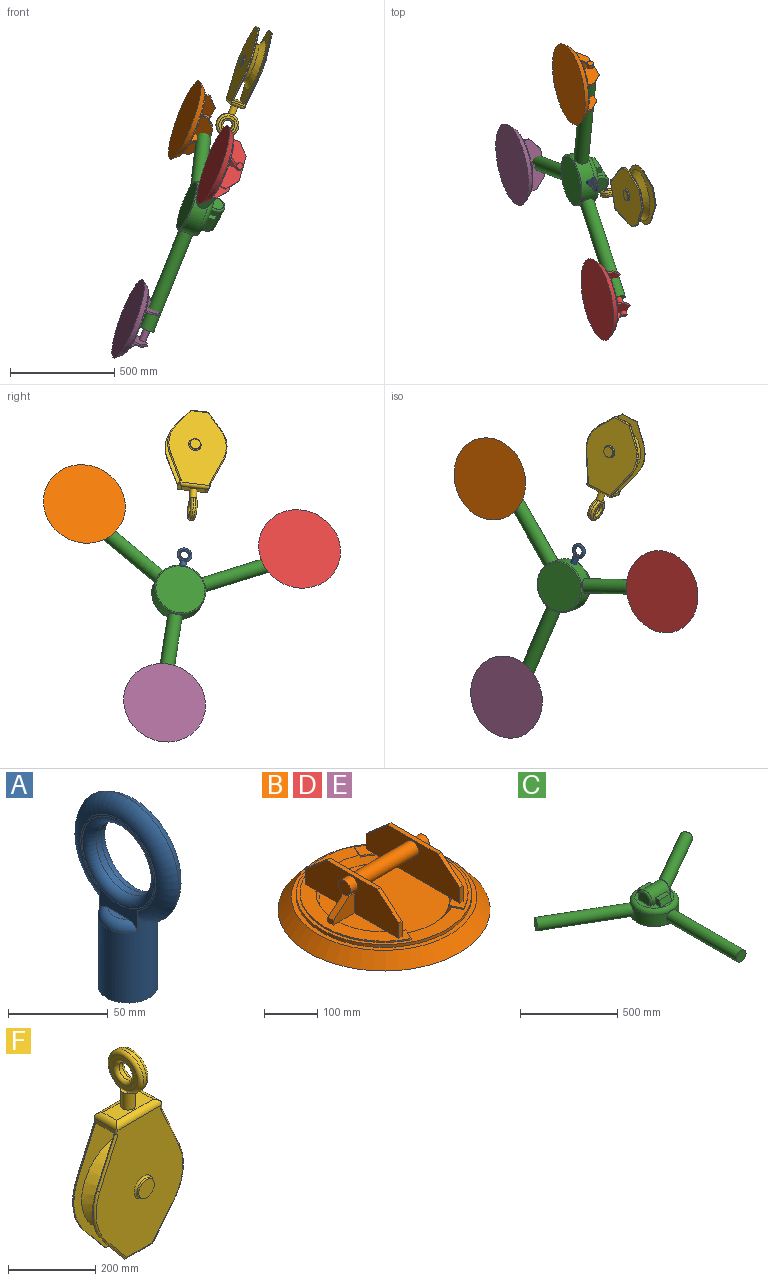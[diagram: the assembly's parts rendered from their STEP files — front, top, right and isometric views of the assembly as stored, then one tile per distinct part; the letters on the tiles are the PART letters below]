
ASSEMBLY  parts=6 mates=6
PART A: 13 faces, bbox 32.5x79x118.5 mm
  f0: plane 14.48x3.1mm, normal (0,0,1), area 31mm2, adj f5,f10
  f1: cylinder r=15mm len=56.07mm, axis (0,0,-1), area 4201.7mm2, adj f3,f4,f5,f7,f8,f9,f10
  f2: plane 14.48x3.1mm, normal (0,0,1), area 31mm2, adj f4,f9
  f3: plane 30x30mm, normal (0,0,-1), area 706.9mm2, adj f1
  f4: plane 62.82x53.03mm, normal (1,0,0), area 344.9mm2, adj f1,f2,f7,f9,f12
  f5: plane 62.82x53.03mm, normal (-1,0,0), area 344.8mm2, adj f0,f1,f8,f10,f11
  f6: cylinder r=20.45mm len=40.9mm, axis (-1,0,0), area 488.3mm2, adj f11,f12
  f7: torus R=26.52mm, axis (1,0,0), area 2157.2mm2, adj f1,f4,f8
  f8: torus R=26.52mm, axis (1,0,0), area 2157.2mm2, adj f1,f5,f7
  f9: torus R=10mm, axis (0,0,1), area 210.8mm2, adj f1,f2,f4
  f10: torus R=10mm, axis (0,0,1), area 210.8mm2, adj f0,f1,f5
  f11: torus R=25.45mm, axis (1,0,0), area 1098.8mm2, adj f5,f6
  f12: torus R=25.45mm, axis (1,0,0), area 1098.8mm2, adj f4,f6
PART B: 50 faces, bbox 400x400x123.8 mm
  f0: plane 34.67x9.11mm, normal (0,1,0), area 316mm2, adj f2,f3,f4,f19
  f1: plane 34.67x9.11mm, normal (0,-1,0), area 316mm2, adj f2,f3,f4,f20
  f2: plane 249.76x84.24mm, normal (1,0,0), area 16662.5mm2, adj f0,f1,f4,f17,f18,f19,f20,f23
  f3: plane 249.76x84.24mm, normal (-1,0,0), area 17354.3mm2, adj f0,f1,f4,f17,f18,f19,f20,f45
  f4: plane 286.37x105.25mm, normal (0,0,1), area 9032.7mm2, adj f0,f1,f2,f3,f12,f13,f14,f15
  f5: plane 330.98x330.98mm, normal (0,0,1), area 13326.7mm2, adj f6,f11,f12,f13,f14,f31,f32,f33
  f6: cone r=134.59mm half-angle=37deg, axis (0,0,1), area 15653.4mm2, adj f5,f7,f16,f35
  f7: plane 245.92x245.92mm, normal (0,0,1), area 47497.9mm2, adj f6
  f8: plane 400x400mm, normal (0,0,-1), area 125663.7mm2, adj f9
  f9: cone r=200mm half-angle=39.8deg, axis (0,0,-1), area 46006.2mm2, adj f8,f10
  f10: plane 350x350mm, normal (0,0,1), area 10175.1mm2, adj f9,f11
  f11: cylinder r=165.49mm len=330.98mm, axis (0,0,1), area 6841.3mm2, adj f5,f10
  f12: plane 26.9x13.27mm, normal (-0.9,-0.44,0), area 90mm2, adj f4,f5,f13,f15,f16
  f13: cylinder r=158.49mm len=286.37mm, axis (0,0,-1), area 1072.7mm2, adj f4,f5,f12,f14
  f14: plane 27.3x12.43mm, normal (-0.91,0.41,0), area 90mm2, adj f4,f5,f13,f15,f16
  f15: cylinder r=128.49mm len=232.17mm, axis (0,0,-1), area 869.6mm2, adj f4,f12,f14,f16,f17
  f16: plane 243.19x81.35mm, normal (0,0,-1), area 1811.1mm2, adj f6,f12,f14,f15
  f17: plane 206x51.68mm, normal (0,0,-1), area 2448.9mm2, adj f2,f3,f15,f24,f25
  f18: plane 134.61x9.11mm, normal (0,0,1), area 1226.8mm2, adj f2,f3,f19,f20
  f19: plane 57.58x49.57mm, normal (0,0.65,0.76), area 692.4mm2, adj f0,f2,f3,f18
  f20: plane 57.58x49.57mm, normal (0,-0.65,0.76), area 692.4mm2, adj f1,f2,f3,f18
  f21: plane 15x10.68mm, normal (1,0,0), area 160.2mm2, adj f4,f22,f24,f25
  f22: plane 41.45x35.44mm, normal (0.65,0,0.76), area 818mm2, adj f21,f23,f24,f25
  f23: plane 15.31x15mm, normal (0,0,1), area 229.7mm2, adj f2,f22,f24,f25
  f24: plane 56.76x46.12mm, normal (0,-1,0), area 1883.2mm2, adj f2,f4,f17,f21,f22,f23
  f25: plane 56.76x46.12mm, normal (0,1,0), area 1883.2mm2, adj f2,f4,f17,f21,f22,f23
  f26: plane 34.67x9.11mm, normal (0,1,0), area 316mm2, adj f28,f29,f30,f38
  f27: plane 34.67x9.11mm, normal (0,-1,0), area 316mm2, adj f28,f29,f30,f39
  f28: plane 249.76x84.24mm, normal (-1,0,0), area 16662.5mm2, adj f26,f27,f30,f36,f37,f38,f39,f42
  f29: plane 249.76x84.24mm, normal (1,0,0), area 17354.3mm2, adj f26,f27,f30,f36,f37,f38,f39,f45
  f30: plane 286.37x105.25mm, normal (0,0,1), area 9032.7mm2, adj f26,f27,f28,f29,f31,f32,f33,f34
  f31: plane 26.9x13.27mm, normal (0.9,-0.44,0), area 90mm2, adj f5,f30,f32,f34,f35
  f32: cylinder r=158.49mm len=286.37mm, axis (0,0,-1), area 1072.7mm2, adj f5,f30,f31,f33
  f33: plane 27.3x12.43mm, normal (0.91,0.41,0), area 90mm2, adj f5,f30,f32,f34,f35
  f34: cylinder r=128.49mm len=232.17mm, axis (0,0,-1), area 869.6mm2, adj f30,f31,f33,f35,f36
  f35: plane 243.19x81.35mm, normal (0,0,-1), area 1811.1mm2, adj f6,f31,f33,f34
  f36: plane 206x51.68mm, normal (0,0,-1), area 2448.9mm2, adj f28,f29,f34,f43,f44
  f37: plane 134.61x9.11mm, normal (0,0,1), area 1226.8mm2, adj f28,f29,f38,f39
  f38: plane 57.58x49.57mm, normal (0,0.65,0.76), area 692.4mm2, adj f26,f28,f29,f37
  f39: plane 57.58x49.57mm, normal (0,-0.65,0.76), area 692.4mm2, adj f27,f28,f29,f37
  f40: plane 15x10.68mm, normal (-1,0,0), area 160.2mm2, adj f30,f41,f43,f44
  f41: plane 41.45x35.44mm, normal (-0.65,0,0.76), area 818mm2, adj f40,f42,f43,f44
  f42: plane 15.31x15mm, normal (0,0,1), area 229.7mm2, adj f28,f41,f43,f44
  f43: plane 56.76x46.12mm, normal (0,-1,0), area 1883.2mm2, adj f28,f30,f36,f40,f41,f42
  f44: plane 56.76x46.12mm, normal (0,1,0), area 1883.2mm2, adj f28,f30,f36,f40,f41,f42
  f45: cylinder r=16.26mm len=153.62mm, axis (-1,0,0), area 15695.3mm2, adj f3,f29
  f46: plane 32.52x32.52mm, normal (-1,0,0), area 830.7mm2, adj f47
  f47: cylinder r=16.26mm len=32.52mm, axis (-1,0,0), area 2051.1mm2, adj f28,f46
  f48: cylinder r=16.26mm len=32.52mm, axis (-1,0,0), area 2051.1mm2, adj f2,f49
  f49: plane 32.52x32.52mm, normal (1,0,0), area 830.7mm2, adj f48
PART C: 24 faces, bbox 1125.9x975.1x175.1 mm
  f0: cylinder r=125mm len=250mm, axis (0,0,-1), area 44515.2mm2, adj f1,f4,f6,f20,f22
  f1: torus R=100mm, axis (0,0,1), area 28361.9mm2, adj f0,f2,f6,f20,f22
  f2: plane 200x200mm, normal (0,0,1), area 11368.9mm2, adj f1,f8,f9,f10,f11,f13,f14,f15
  f3: plane 240x240mm, normal (0,0,-1), area 45238.9mm2, adj f4
  f4: torus R=120mm, axis (0,0,1), area 6078.8mm2, adj f0,f3
  f5: plane 69.5x69.5mm, normal (0,-1,0), area 3793.5mm2, adj f6
  f6: cylinder r=34.75mm len=509.93mm, axis (0,1,0), area 110799.7mm2, adj f0,f1,f5
  f7: plane 78x27.87mm, normal (0,0,1), area 2174.1mm2, adj f8,f9,f10,f11
  f8: plane 78x36.94mm, normal (0,-0.94,0.33), area 3056.5mm2, adj f2,f7,f9,f10
  f9: plane 42.16x36.94mm, normal (1,0,0), area 1205.7mm2, adj f2,f7,f8,f11
  f10: plane 42.16x36.94mm, normal (-1,0,0), area 1205.7mm2, adj f2,f7,f8,f11
  f11: cylinder r=50mm len=128mm, axis (-1,0,0), area 19467.6mm2, adj f2,f7,f9,f10,f12,f14,f15,f18
  f12: plane 78x27.87mm, normal (0,0,1), area 2174.1mm2, adj f11,f13,f14,f15
  f13: plane 78x36.94mm, normal (0,0.94,0.33), area 3056.5mm2, adj f2,f12,f14,f15
  f14: plane 42.16x36.94mm, normal (1,0,0), area 1205.7mm2, adj f2,f11,f12,f13
  f15: plane 42.16x36.94mm, normal (-1,0,0), area 1205.7mm2, adj f2,f11,f12,f13
  f16: plane 80x60mm, normal (1,0,0), area 4043.9mm2, adj f2,f19
  f17: plane 80x60mm, normal (-1,0,0), area 4043.9mm2, adj f2,f18
  f18: torus R=40mm, axis (1,0,0), area 2938.1mm2, adj f2,f11,f17
  f19: torus R=40mm, axis (1,0,0), area 2938.1mm2, adj f2,f11,f16
  f20: cylinder r=34.75mm len=476.36mm, axis (0.87,-0.5,0), area 110799.6mm2, adj f0,f1,f21
  f21: plane 69.5x60.19mm, normal (-0.87,0.5,0), area 3793.5mm2, adj f20
  f22: cylinder r=34.75mm len=476.36mm, axis (-0.87,-0.5,0), area 110799.7mm2, adj f0,f1,f23
  f23: plane 69.5x60.19mm, normal (0.87,0.5,0), area 3793.5mm2, adj f22
PART D: same geometry as B
PART E: same geometry as B
PART F: 67 faces, bbox 313.9x118.5x549.6 mm
  f0: cylinder r=54.75mm len=31.96mm, axis (-1,0,0), area 278.3mm2, adj f2,f8
  f1: cylinder r=54.75mm len=31.96mm, axis (-1,0,0), area 278.3mm2, adj f2,f10
  f2: cylinder r=16.74mm len=47.87mm, axis (0,0,-1), area 4897.8mm2, adj f0,f1,f3,f42
  f3: cylinder r=54.75mm len=109.5mm, axis (-1,0,0), area 3105.1mm2, adj f2,f8,f10
  f4: cylinder r=23.34mm len=46.68mm, axis (-1,0,0), area 1466.5mm2, adj f7,f9
  f5: plane 89.5x89.5mm, normal (1,0,0), area 2799.5mm2, adj f9,f10
  f6: plane 89.5x89.5mm, normal (-1,0,0), area 2799.5mm2, adj f7,f8
  f7: torus R=33.34mm, axis (1,0,0), area 2662.2mm2, adj f4,f6
  f8: torus R=44.75mm, axis (1,0,0), area 5045.1mm2, adj f0,f3,f6
  f9: torus R=33.34mm, axis (1,0,0), area 2662.2mm2, adj f4,f5
  f10: torus R=44.75mm, axis (1,0,0), area 5045.1mm2, adj f1,f3,f5
  f11: plane 250x250mm, normal (0,1,0), area 47087mm2, adj f14,f36
  f12: plane 250x250mm, normal (0,-1,0), area 47087mm2, adj f13,f24
  f13: cone r=125mm half-angle=54.5deg, axis (0,-1,0), area 29199.9mm2, adj f12,f14
  f14: cone r=125mm half-angle=54.5deg, axis (0,1,0), area 29199.9mm2, adj f11,f13
  f15: plane 131.07x58.17mm, normal (-0.91,0,0.41), area 286.8mm2, adj f16,f23,f41,f48
  f16: cylinder r=145mm len=150.44mm, axis (0,1,0), area 319.5mm2, adj f15,f17,f23,f49
  f17: plane 83.79x68.31mm, normal (-0.78,0,-0.63), area 216.2mm2, adj f16,f18,f23,f50
  f18: plane 88.15x2mm, normal (0,0,-1), area 176.3mm2, adj f17,f19,f23,f51
  f19: plane 83.79x68.31mm, normal (0.78,0,-0.63), area 216.2mm2, adj f18,f20,f23,f52
  f20: cylinder r=145mm len=150.44mm, axis (0,1,0), area 319.5mm2, adj f19,f21,f23,f53
  f21: plane 131.07x58.17mm, normal (0.91,0,0.41), area 286.8mm2, adj f20,f23,f40,f54
  f22: plane 370.3x280mm, normal (0,-1,0), area 75486.2mm2, adj f44,f47,f48,f49,f50,f51,f52,f53
  f23: plane 365.3x290mm, normal (0,1,0), area 79482.6mm2, adj f15,f16,f17,f18,f19,f20,f21,f24
  f24: cylinder r=25.23mm len=50.47mm, axis (0,1,0), area 773.3mm2, adj f12,f23
  f25: plane 50.47x50.47mm, normal (0,-1,0), area 2000.4mm2, adj f26
  f26: cylinder r=25.23mm len=50.47mm, axis (0,1,0), area 792.7mm2, adj f25,f66
  f27: plane 131.07x58.17mm, normal (-0.91,0,0.41), area 286.8mm2, adj f28,f35,f41,f57
  f28: cylinder r=145mm len=150.44mm, axis (0,-1,0), area 319.5mm2, adj f27,f29,f35,f58
  f29: plane 83.79x68.31mm, normal (-0.78,0,-0.63), area 216.2mm2, adj f28,f30,f35,f59
  f30: plane 88.15x2mm, normal (0,0,-1), area 176.3mm2, adj f29,f31,f35,f60
  f31: plane 83.79x68.31mm, normal (0.78,0,-0.63), area 216.2mm2, adj f30,f32,f35,f61
  f32: cylinder r=145mm len=150.44mm, axis (0,-1,0), area 319.5mm2, adj f31,f33,f35,f62
  f33: plane 131.07x58.17mm, normal (0.91,0,0.41), area 286.8mm2, adj f32,f35,f40,f63
  f34: plane 370.3x280mm, normal (0,1,0), area 75486.2mm2, adj f45,f56,f57,f58,f59,f60,f61,f62
  f35: plane 365.3x290mm, normal (0,-1,0), area 79482.6mm2, adj f27,f28,f29,f30,f31,f32,f33,f36
  f36: cylinder r=25.23mm len=50.47mm, axis (0,-1,0), area 773.3mm2, adj f11,f35
  f37: plane 50.47x50.47mm, normal (0,1,0), area 2000.4mm2, adj f38
  f38: cylinder r=25.23mm len=50.47mm, axis (0,-1,0), area 792.7mm2, adj f37,f65
  f39: plane 148.73x60mm, normal (0,0,-1), area 8924mm2, adj f23,f35,f40,f41
  f40: plane 64x10mm, normal (1,0,0), area 640mm2, adj f21,f33,f39,f43,f55,f64
  f41: plane 64x10mm, normal (-1,0,0), area 640mm2, adj f15,f27,f39,f46,f47,f56
  f42: plane 118.73x44mm, normal (0,0,1), area 4343.4mm2, adj f2,f43,f44,f45,f46
  f43: cylinder r=15mm len=71.07mm, axis (0,-1,0), area 1451.2mm2, adj f40,f42,f44,f45,f55,f64
  f44: cylinder r=15mm len=145.81mm, axis (1,0,0), area 3212.1mm2, adj f22,f42,f43,f46,f47,f55
  f45: cylinder r=15mm len=145.81mm, axis (1,0,0), area 3212.1mm2, adj f34,f42,f43,f46,f56,f64
  f46: cylinder r=15mm len=71.07mm, axis (0,1,0), area 1451.2mm2, adj f41,f42,f44,f45,f47,f56
  f47: cylinder r=5mm len=17.52mm, axis (0,0,-1), area 107.6mm2, adj f22,f41,f44,f46,f48
  f48: cylinder r=5mm len=134.07mm, axis (0.41,0,0.91), area 1129.3mm2, adj f15,f22,f47,f49
  f49: torus R=140mm, axis (0,-1,0), area 1238.9mm2, adj f16,f22,f48,f50
  f50: cylinder r=5mm len=86.95mm, axis (-0.63,0,0.78), area 842.3mm2, adj f17,f22,f49,f51
  f51: cylinder r=5mm len=88.15mm, axis (-1,0,0), area 678.8mm2, adj f18,f22,f50,f52
  f52: cylinder r=5mm len=86.95mm, axis (-0.63,0,-0.78), area 842.3mm2, adj f19,f22,f51,f53
  f53: torus R=140mm, axis (0,-1,0), area 1238.9mm2, adj f20,f22,f52,f54
  f54: cylinder r=5mm len=134.07mm, axis (0.41,0,-0.91), area 1129.3mm2, adj f21,f22,f53,f55
  f55: cylinder r=5mm len=17.52mm, axis (0,0,-1), area 107.6mm2, adj f22,f40,f43,f44,f54
  f56: cylinder r=5mm len=17.52mm, axis (0,0,-1), area 107.6mm2, adj f34,f41,f45,f46,f57
  f57: cylinder r=5mm len=134.07mm, axis (0.41,0,0.91), area 1129.3mm2, adj f27,f34,f56,f58
  f58: torus R=140mm, axis (0,1,0), area 1238.9mm2, adj f28,f34,f57,f59
  f59: cylinder r=5mm len=86.95mm, axis (-0.63,0,0.78), area 842.3mm2, adj f29,f34,f58,f60
  f60: cylinder r=5mm len=88.15mm, axis (-1,0,0), area 678.8mm2, adj f30,f34,f59,f61
  f61: cylinder r=5mm len=86.95mm, axis (-0.63,0,-0.78), area 842.3mm2, adj f31,f34,f60,f62
  f62: torus R=140mm, axis (0,1,0), area 1238.9mm2, adj f32,f34,f61,f63
  f63: cylinder r=5mm len=134.07mm, axis (0.41,0,-0.91), area 1129.3mm2, adj f33,f34,f62,f64
  f64: cylinder r=5mm len=17.52mm, axis (0,0,-1), area 107.6mm2, adj f34,f40,f43,f45,f63
  f65: torus R=30.23mm, axis (0,1,0), area 1334.9mm2, adj f34,f38
  f66: torus R=30.23mm, axis (0,-1,0), area 1334.9mm2, adj f22,f26
PLACE A rot(axis=(0.41,0.83,0.38),25.2deg) t=(277.11,-2786.84,1282.16)mm
PLACE B rot(axis=(0.72,0.41,0.56),159.7deg) t=(182.61,-2318.17,1599.43)mm
PLACE C rot(axis=(-0.82,0.22,-0.53),149.6deg) t=(233.8,-2770.11,1174.48)mm
PLACE D rot(axis=(-0.77,0.45,-0.46),134.6deg) t=(320.02,-3349.91,1383.87)mm
PLACE E rot(axis=(0,0.99,0.15),111.7deg) t=(-88.67,-2702.71,646.35)mm
PLACE F rot(axis=(-0.64,-0.77,0.09),161.8deg) t=(499.65,-2853.7,1869.84)mm
MATE cylindrical A.f1 <-> C.f20  axis (-0.37,0.14,-0.92) through (287.53,-2790.86,1308.06)mm
MATE parallel C.f0 <-> F.f22  axis (-0.92,-0.19,0.34) through (192.39,-2778.82,1189.78)mm
MATE parallel C.f22 <-> D.f45  axis (0.3,-0.91,0.28) through (420.67,-3344.63,1353.09)mm
MATE parallel C.f0 <-> D.f6  axis (-0.92,-0.19,0.34) through (192.39,-2778.82,1189.78)mm
MATE planar A.f4 <-> C.f0  axis (0.92,0.19,-0.34) through (307.42,-2794.76,1339.38)mm
MATE cylindrical D.f45 <-> C.f22  axis (-0.3,0.91,-0.28) through (390.35,-3251.39,1324.1)mm
